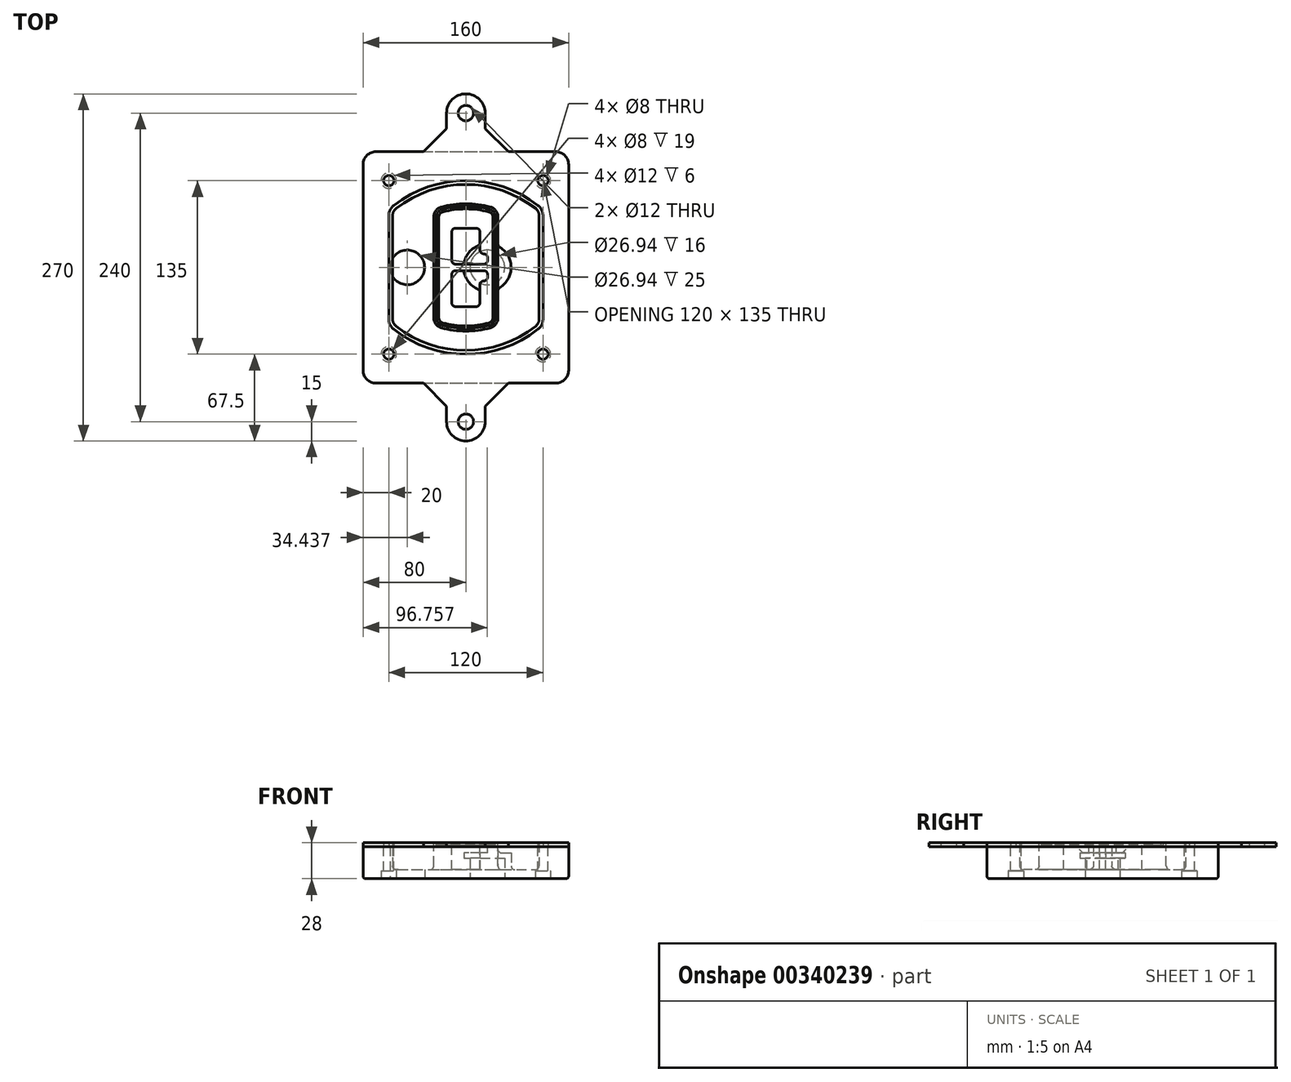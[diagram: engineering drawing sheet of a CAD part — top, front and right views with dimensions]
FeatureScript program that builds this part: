
annotation { "Feature Type Name" : "Feature", "Feature Type Description" : "" }
export const myFeature = defineFeature(function(context is Context, id is Id, definition is map)
    precondition{}
    {
        {
            var Q0;
            Q0=qCreatedBy(makeId("Top.planeOp"),FACE);
            var sketch = newSketch(context, id + "F0", { "sketchPlane" : qUnion([Q0])});
            skPoint(sketch, "E0.rect.middle", {"position": v(0, 0) * mm});
            skLineSegment(sketch, "E1.bottom", {"start": v(-70, -90) * mm, "end": v(70, -90) * mm});
            skLineSegment(sketch, "E1.top", {"start": v(-70, 90) * mm, "end": v(70, 90) * mm});
            skLineSegment(sketch, "E1.left", {"start": v(-80, -80) * mm, "end": v(-80, 80) * mm});
            skLineSegment(sketch, "E1.right", {"start": v(80, -80) * mm, "end": v(80, 80) * mm});
            skLineSegment(sketch, "E2", {"start": v(-80, 90) * mm, "end": v(80, -90) * mm, "construction": true});
            skLineSegment(sketch, "E3", {"start": v(80, 90) * mm, "end": v(-80, -90) * mm, "construction": true});
            skCircle(sketch, "E4", {"center": v(-60, 67.5) * mm, "radius": 4 * mm});
            skCircle(sketch, "E5", {"center": v(60, 67.5) * mm, "radius": 4 * mm});
            skCircle(sketch, "E6", {"center": v(60, -67.5) * mm, "radius": 4 * mm});
            skCircle(sketch, "E7", {"center": v(-60, -67.5) * mm, "radius": 4 * mm});
            skLineSegment(sketch, "E8", {"start": v(-60, 67.5) * mm, "end": v(60, 67.5) * mm, "construction": true});
            skLineSegment(sketch, "E9", {"start": v(60, 67.5) * mm, "end": v(60, -67.5) * mm, "construction": true});
            skLineSegment(sketch, "E10", {"start": v(60, -67.5) * mm, "end": v(-60, -67.5) * mm, "construction": true});
            skLineSegment(sketch, "E11", {"start": v(-60, -67.5) * mm, "end": v(-60, 67.5) * mm, "construction": true});
            skLineSegment(sketch, "E12", {"start": v(-60, 40.3) * mm, "end": v(-60, -40.3) * mm});
            skLineSegment(sketch, "E13", {"start": v(60, 40.3) * mm, "end": v(60, -40.3) * mm});
            skArc(sketch, "E14", {"start": v(56.15, 48.18) * mm, "mid": v(0, 67.5) * mm, "end": v(-56.15, 48.18) * mm});
            skArc(sketch, "E15", {"start": v(-56.15, -48.18) * mm, "mid": v(0, -67.5) * mm, "end": v(56.15, -48.18) * mm});
            skLineSegment(sketch, "E16", {"start": v(-60, 0) * mm, "end": v(60, 0) * mm, "construction": true});
            skPoint(sketch, "E17.visualSharp", {"position": v(-60, -45) * mm});
            skArc(sketch, "E17.filletArc", {"start": v(-60, -40.3) * mm, "mid": v(-58.99, -44.68) * mm, "end": v(-56.15, -48.18) * mm});
            skPoint(sketch, "E18.visualSharp", {"position": v(-60, 45) * mm});
            skArc(sketch, "E18.filletArc", {"start": v(-56.15, 48.18) * mm, "mid": v(-58.99, 44.68) * mm, "end": v(-60, 40.3) * mm});
            skPoint(sketch, "E19.visualSharp", {"position": v(60, 45) * mm});
            skArc(sketch, "E19.filletArc", {"start": v(60, 40.3) * mm, "mid": v(58.99, 44.68) * mm, "end": v(56.15, 48.18) * mm});
            skPoint(sketch, "E20.visualSharp", {"position": v(60, -45) * mm});
            skArc(sketch, "E20.filletArc", {"start": v(56.15, -48.18) * mm, "mid": v(58.99, -44.68) * mm, "end": v(60, -40.3) * mm});
            skPoint(sketch, "E21.visualSharp", {"position": v(-80, 90) * mm});
            skArc(sketch, "E21.filletArc", {"start": v(-70, 90) * mm, "mid": v(-77.07, 87.07) * mm, "end": v(-80, 80) * mm});
            skPoint(sketch, "E22.visualSharp", {"position": v(80, 90) * mm});
            skArc(sketch, "E22.filletArc", {"start": v(80, 80) * mm, "mid": v(77.07, 87.07) * mm, "end": v(70, 90) * mm});
            skPoint(sketch, "E23.visualSharp", {"position": v(80, -90) * mm});
            skArc(sketch, "E23.filletArc", {"start": v(70, -90) * mm, "mid": v(77.07, -87.07) * mm, "end": v(80, -80) * mm});
            skPoint(sketch, "E24.visualSharp", {"position": v(-80, -90) * mm});
            skArc(sketch, "E24.filletArc", {"start": v(-80, -80) * mm, "mid": v(-77.07, -87.07) * mm, "end": v(-70, -90) * mm});
            skArc(sketch, "E25.0", {"start": v(57, 40.3) * mm, "mid": v(56.3, 43.36) * mm, "end": v(54.3, 45.81) * mm});
            skLineSegment(sketch, "E25.1", {"start": v(57, 40.3) * mm, "end": v(57, -40.3) * mm});
            skArc(sketch, "E25.2", {"start": v(54.3, -45.81) * mm, "mid": v(56.3, -43.36) * mm, "end": v(57, -40.3) * mm});
            skArc(sketch, "E25.3", {"start": v(-54.3, -45.81) * mm, "mid": v(0, -64.5) * mm, "end": v(54.3, -45.81) * mm});
            skArc(sketch, "E25.4", {"start": v(-57, -40.3) * mm, "mid": v(-56.3, -43.36) * mm, "end": v(-54.3, -45.81) * mm});
            skArc(sketch, "E25.5", {"start": v(54.3, 45.81) * mm, "mid": v(0, 64.5) * mm, "end": v(-54.3, 45.81) * mm});
            skLineSegment(sketch, "E25.6", {"start": v(-57, 40.3) * mm, "end": v(-57, -40.3) * mm});
            skArc(sketch, "E25.7", {"start": v(-54.3, 45.81) * mm, "mid": v(-56.3, 43.36) * mm, "end": v(-57, 40.3) * mm});
            skArc(sketch, "E26.0", {"start": v(-58.62, 51.33) * mm, "mid": v(-62.58, 46.43) * mm, "end": v(-64, 40.3) * mm});
            skArc(sketch, "E26.1", {"start": v(58.62, 51.33) * mm, "mid": v(0, 71.5) * mm, "end": v(-58.62, 51.33) * mm});
            skArc(sketch, "E26.2", {"start": v(64, 40.3) * mm, "mid": v(62.58, 46.43) * mm, "end": v(58.62, 51.33) * mm});
            skLineSegment(sketch, "E26.3", {"start": v(64, 40.3) * mm, "end": v(64, -40.3) * mm});
            skArc(sketch, "E26.4", {"start": v(58.62, -51.33) * mm, "mid": v(62.58, -46.43) * mm, "end": v(64, -40.3) * mm});
            skLineSegment(sketch, "E26.5", {"start": v(-64, 40.3) * mm, "end": v(-64, -40.3) * mm});
            skArc(sketch, "E26.6", {"start": v(-58.62, -51.33) * mm, "mid": v(0, -71.5) * mm, "end": v(58.62, -51.33) * mm});
            skArc(sketch, "E26.7", {"start": v(-64, -40.3) * mm, "mid": v(-62.58, -46.43) * mm, "end": v(-58.62, -51.33) * mm});
            skSolve(sketch);
        }
        {
            var Q0;
            Q0=makeQuery(id+"F0.imprint","IMPRINT",FACE,{"disambiguationData":[TD([[makeQuery(id+"F0.imprint","IMPRINT",EDGE,{"derivedFrom":sQuery(id+"F0.wireOp",EDGE,"E1.bottom")}),1.0]])]});
            var Q1;
            Q1=makeQuery(id+"F0.imprint","IMPRINT",FACE,{"disambiguationData":[TD([[makeQuery(id+"F0.imprint","IMPRINT",EDGE,{"derivedFrom":sQuery(id+"F0.wireOp",EDGE,"E12")}),1.0]])]});
            var Q2;
            Q2=makeQuery(id+"F0.imprint","IMPRINT",FACE,{"disambiguationData":[TD([[makeQuery(id+"F0.imprint","IMPRINT",EDGE,{"derivedFrom":sQuery(id+"F0.wireOp",EDGE,"E25.0")}),1.0]])]});
            var Q3;
            Q3=makeQuery(id+"F0.imprint","IMPRINT",FACE,{"disambiguationData":[TD([[makeQuery(id+"F0.imprint","IMPRINT",EDGE,{"derivedFrom":sQuery(id+"F0.wireOp",EDGE,"E12")}),-1.0]])]});
            extrude(context, id + "F1", {"entities" : qUnion([Q0, Q1, Q2, Q3]), "oppositeDirection" : true, "depth" : 25 * mm});
        }
        {
            var Q0;
            Q0=makeQuery(id+"F0.imprint","IMPRINT",FACE,{"disambiguationData":[TD([[makeQuery(id+"F0.imprint","IMPRINT",EDGE,{"derivedFrom":sQuery(id+"F0.wireOp",EDGE,"E12")}),1.0]])]});
            extrude(context, id + "F2", {"entities" : qUnion([Q0]), "operationType" : NewBodyOperationType.ADD, "depth" : 3 * mm});
        }
        {
            var Q0;
            Q0=makeQuery(id+"F0.imprint","IMPRINT",FACE,{"disambiguationData":[TD([[makeQuery(id+"F0.imprint","IMPRINT",EDGE,{"derivedFrom":sQuery(id+"F0.wireOp",EDGE,"E25.0")}),1.0]])]});
            extrude(context, id + "F3", {"entities" : qUnion([Q0]), "operationType" : NewBodyOperationType.REMOVE, "oppositeDirection" : true, "depth" : 18 * mm});
        }
        {
            var Q0;
            Q0=makeQuery(id+"F2.opExtrude","CAP_FACE",FACE,{"disambiguationData":[OSD([sQuery(id+"F0.wireOp",EDGE,"E12"),sQuery(id+"F0.wireOp",EDGE,"E13"),sQuery(id+"F0.wireOp",EDGE,"E14"),sQuery(id+"F0.wireOp",EDGE,"E15"),sQuery(id+"F0.wireOp",EDGE,"E17.filletArc"),sQuery(id+"F0.wireOp",EDGE,"E18.filletArc"),sQuery(id+"F0.wireOp",EDGE,"E19.filletArc"),sQuery(id+"F0.wireOp",EDGE,"E20.filletArc"),sQuery(id+"F0.wireOp",EDGE,"E25.0"),sQuery(id+"F0.wireOp",EDGE,"E25.1"),sQuery(id+"F0.wireOp",EDGE,"E25.2"),sQuery(id+"F0.wireOp",EDGE,"E25.3"),sQuery(id+"F0.wireOp",EDGE,"E25.4"),sQuery(id+"F0.wireOp",EDGE,"E25.5"),sQuery(id+"F0.wireOp",EDGE,"E25.6"),sQuery(id+"F0.wireOp",EDGE,"E25.7")])],"isStart":false});
            var sketch = newSketch(context, id + "F4", { "sketchPlane" : qUnion([Q0])});
            skArc(sketch, "E27.0", {"start": v(-19.08, -46.97) * mm, "mid": v(0, -49.5) * mm, "end": v(19.08, -46.97) * mm});
            skArc(sketch, "E28.0", {"start": v(19.08, 46.97) * mm, "mid": v(0, 49.5) * mm, "end": v(-19.08, 46.97) * mm});
            skLineSegment(sketch, "E29", {"start": v(-25, 39.25) * mm, "end": v(-25, -39.25) * mm});
            skLineSegment(sketch, "E30", {"start": v(25, 39.25) * mm, "end": v(25, -39.25) * mm});
            skLineSegment(sketch, "E31", {"start": v(-25, 45.1) * mm, "end": v(25, 45.1) * mm, "construction": true});
            skLineSegment(sketch, "E32", {"start": v(-25, -45.1) * mm, "end": v(25, -45.1) * mm, "construction": true});
            skPoint(sketch, "E33.visualSharp", {"position": v(-25, 45.1) * mm});
            skArc(sketch, "E33.filletArc", {"start": v(-19.08, 46.97) * mm, "mid": v(-23.35, 44.11) * mm, "end": v(-25, 39.25) * mm});
            skPoint(sketch, "E34.visualSharp", {"position": v(25, 45.1) * mm});
            skArc(sketch, "E34.filletArc", {"start": v(25, 39.25) * mm, "mid": v(23.35, 44.11) * mm, "end": v(19.08, 46.97) * mm});
            skPoint(sketch, "E35.visualSharp", {"position": v(25, -45.1) * mm});
            skArc(sketch, "E35.filletArc", {"start": v(19.08, -46.97) * mm, "mid": v(23.35, -44.11) * mm, "end": v(25, -39.25) * mm});
            skPoint(sketch, "E36.visualSharp", {"position": v(-25, -45.1) * mm});
            skArc(sketch, "E36.filletArc", {"start": v(-25, -39.25) * mm, "mid": v(-23.35, -44.11) * mm, "end": v(-19.08, -46.97) * mm});
            skArc(sketch, "E37.0", {"start": v(54.3, 45.81) * mm, "mid": v(0, 64.5) * mm, "end": v(-54.3, 45.81) * mm});
            skArc(sketch, "E37.1", {"start": v(-54.3, 45.81) * mm, "mid": v(-56.3, 43.36) * mm, "end": v(-57, 40.3) * mm});
            skLineSegment(sketch, "E37.2", {"start": v(-57, 40.3) * mm, "end": v(-57, -40.3) * mm});
            skArc(sketch, "E37.3", {"start": v(-57, -40.3) * mm, "mid": v(-56.3, -43.36) * mm, "end": v(-54.3, -45.81) * mm});
            skArc(sketch, "E37.4", {"start": v(-54.3, -45.81) * mm, "mid": v(0, -64.5) * mm, "end": v(54.3, -45.81) * mm});
            skArc(sketch, "E37.5", {"start": v(54.3, -45.81) * mm, "mid": v(56.3, -43.36) * mm, "end": v(57, -40.3) * mm});
            skLineSegment(sketch, "E37.6", {"start": v(57, 40.3) * mm, "end": v(57, -40.3) * mm});
            skArc(sketch, "E37.7", {"start": v(57, 40.3) * mm, "mid": v(56.3, 43.36) * mm, "end": v(54.3, 45.81) * mm});
            skLineSegment(sketch, "E38.0", {"start": v(23, 39.25) * mm, "end": v(23, -39.25) * mm});
            skArc(sketch, "E38.1", {"start": v(18.56, -45.04) * mm, "mid": v(21.76, -42.9) * mm, "end": v(23, -39.25) * mm});
            skArc(sketch, "E38.2", {"start": v(-18.56, -45.04) * mm, "mid": v(0, -47.5) * mm, "end": v(18.56, -45.04) * mm});
            skArc(sketch, "E38.3", {"start": v(-23, -39.25) * mm, "mid": v(-21.76, -42.9) * mm, "end": v(-18.56, -45.04) * mm});
            skLineSegment(sketch, "E38.4", {"start": v(-23, 39.25) * mm, "end": v(-23, -39.25) * mm});
            skArc(sketch, "E38.5", {"start": v(23, 39.25) * mm, "mid": v(21.76, 42.9) * mm, "end": v(18.56, 45.04) * mm});
            skArc(sketch, "E38.6", {"start": v(-18.56, 45.04) * mm, "mid": v(-21.76, 42.9) * mm, "end": v(-23, 39.25) * mm});
            skArc(sketch, "E38.7", {"start": v(18.56, 45.04) * mm, "mid": v(0, 47.5) * mm, "end": v(-18.56, 45.04) * mm});
            skArc(sketch, "E39.0", {"start": v(21, 39.25) * mm, "mid": v(20.18, 41.68) * mm, "end": v(18.04, 43.1) * mm});
            skLineSegment(sketch, "E39.1", {"start": v(21, 39.25) * mm, "end": v(21, -39.25) * mm});
            skArc(sketch, "E39.2", {"start": v(18.04, -43.1) * mm, "mid": v(20.18, -41.68) * mm, "end": v(21, -39.25) * mm});
            skArc(sketch, "E39.3", {"start": v(-18.04, -43.1) * mm, "mid": v(0, -45.5) * mm, "end": v(18.04, -43.1) * mm});
            skArc(sketch, "E39.4", {"start": v(-21, -39.25) * mm, "mid": v(-20.18, -41.68) * mm, "end": v(-18.04, -43.1) * mm});
            skArc(sketch, "E39.5", {"start": v(18.04, 43.1) * mm, "mid": v(0, 45.5) * mm, "end": v(-18.04, 43.1) * mm});
            skLineSegment(sketch, "E39.6", {"start": v(-21, 39.25) * mm, "end": v(-21, -39.25) * mm});
            skArc(sketch, "E39.7", {"start": v(-18.04, 43.1) * mm, "mid": v(-20.18, 41.68) * mm, "end": v(-21, 39.25) * mm});
            skLineSegment(sketch, "E40", {"start": v(-25, 0) * mm, "end": v(25, 0) * mm, "construction": true});
            skLineSegment(sketch, "E41", {"start": v(-11, 5.5) * mm, "end": v(-11, 27.5) * mm});
            skLineSegment(sketch, "E42", {"start": v(-8, 30.5) * mm, "end": v(8, 30.5) * mm});
            skLineSegment(sketch, "E43", {"start": v(11, 27.5) * mm, "end": v(11, 13.5) * mm});
            skLineSegment(sketch, "E44", {"start": v(14, 10.5) * mm, "end": v(14, 10.5) * mm});
            skLineSegment(sketch, "E45", {"start": v(17, 7.5) * mm, "end": v(17, 5.5) * mm});
            skLineSegment(sketch, "E46", {"start": v(14, 2.5) * mm, "end": v(-8, 2.5) * mm});
            skPoint(sketch, "E47.visualSharp", {"position": v(-11, 30.5) * mm});
            skArc(sketch, "E47.filletArc", {"start": v(-8, 30.5) * mm, "mid": v(-10.12, 29.62) * mm, "end": v(-11, 27.5) * mm});
            skPoint(sketch, "E48.visualSharp", {"position": v(11, 30.5) * mm});
            skArc(sketch, "E48.filletArc", {"start": v(11, 27.5) * mm, "mid": v(10.12, 29.62) * mm, "end": v(8, 30.5) * mm});
            skPoint(sketch, "E49.visualSharp", {"position": v(11, 10.5) * mm});
            skArc(sketch, "E49.filletArc", {"start": v(11, 13.5) * mm, "mid": v(11.88, 11.38) * mm, "end": v(14, 10.5) * mm});
            skPoint(sketch, "E50.visualSharp", {"position": v(17, 10.5) * mm});
            skArc(sketch, "E50.filletArc", {"start": v(17, 7.5) * mm, "mid": v(16.12, 9.62) * mm, "end": v(14, 10.5) * mm});
            skPoint(sketch, "E51.visualSharp", {"position": v(17, 2.5) * mm});
            skArc(sketch, "E51.filletArc", {"start": v(14, 2.5) * mm, "mid": v(16.12, 3.38) * mm, "end": v(17, 5.5) * mm});
            skPoint(sketch, "E52.visualSharp", {"position": v(-11, 2.5) * mm});
            skArc(sketch, "E52.filletArc", {"start": v(-11, 5.5) * mm, "mid": v(-10.12, 3.38) * mm, "end": v(-8, 2.5) * mm});
            skLineSegment(sketch, "E53.0.MirrorCS", {"start": v(14, -2.5) * mm, "end": v(-8, -2.5) * mm});
            skArc(sketch, "E54.0.MirrorCS", {"start": v(-11, -5.5) * mm, "mid": v(-10.12, -3.38) * mm, "end": v(-8, -2.5) * mm});
            skLineSegment(sketch, "E55.0.MirrorCS", {"start": v(-11, -5.5) * mm, "end": v(-11, -27.5) * mm});
            skArc(sketch, "E56.0.MirrorCS", {"start": v(-8, -30.5) * mm, "mid": v(-10.12, -29.62) * mm, "end": v(-11, -27.5) * mm});
            skLineSegment(sketch, "E57.0.MirrorCS", {"start": v(-8, -30.5) * mm, "end": v(8, -30.5) * mm});
            skArc(sketch, "E58.0.MirrorCS", {"start": v(11, -27.5) * mm, "mid": v(10.12, -29.62) * mm, "end": v(8, -30.5) * mm});
            skLineSegment(sketch, "E59.0.MirrorCS", {"start": v(11, -27.5) * mm, "end": v(11, -13.5) * mm});
            skArc(sketch, "E60.0.MirrorCS", {"start": v(11, -13.5) * mm, "mid": v(11.88, -11.38) * mm, "end": v(14, -10.5) * mm});
            skArc(sketch, "E61.0.MirrorCS", {"start": v(17, -7.5) * mm, "mid": v(16.12, -9.62) * mm, "end": v(14, -10.5) * mm});
            skLineSegment(sketch, "E62.0.MirrorCS", {"start": v(17, -7.5) * mm, "end": v(17, -5.5) * mm});
            skArc(sketch, "E63.0.MirrorCS", {"start": v(14, -2.5) * mm, "mid": v(16.12, -3.38) * mm, "end": v(17, -5.5) * mm});
            skSolve(sketch);
        }
        {
            var Q0;
            Q0=makeQuery(id+"F4.imprint","IMPRINT",FACE,{"disambiguationData":[TD([[makeQuery(id+"F4.imprint","IMPRINT",EDGE,{"derivedFrom":sQuery(id+"F4.wireOp",EDGE,"E27.0")}),1.0]])]});
            var Q1;
            Q1=makeQuery(id+"F4.imprint","IMPRINT",FACE,{"disambiguationData":[TD([[makeQuery(id+"F4.imprint","IMPRINT",EDGE,{"derivedFrom":sQuery(id+"F4.wireOp",EDGE,"E38.0")}),-1.0]])]});
            var Q2;
            Q2=makeQuery(id+"F4.imprint","IMPRINT",FACE,{"disambiguationData":[TD([[makeQuery(id+"F4.imprint","IMPRINT",EDGE,{"derivedFrom":sQuery(id+"F4.wireOp",EDGE,"E39.0")}),1.0]])]});
            extrude(context, id + "F5", {"entities" : qUnion([Q0, Q1, Q2]), "operationType" : NewBodyOperationType.ADD, "endBound" : BoundingType.UP_TO_NEXT, "oppositeDirection" : true, "depth" : 25 * mm});
        }
        {
            var Q0;
            Q0=makeQuery(id+"F4.imprint","IMPRINT",FACE,{"disambiguationData":[TD([[makeQuery(id+"F4.imprint","IMPRINT",EDGE,{"derivedFrom":sQuery(id+"F4.wireOp",EDGE,"E38.0")}),-1.0]])]});
            extrude(context, id + "F6", {"entities" : qUnion([Q0]), "operationType" : NewBodyOperationType.REMOVE, "oppositeDirection" : true, "depth" : 2 * mm});
        }
        {
            var Q0;
            Q0=makeQuery(id+"F1.opExtrude","CAP_FACE",FACE,{"disambiguationData":[OSD([sQuery(id+"F0.wireOp",EDGE,"E1.bottom"),sQuery(id+"F0.wireOp",EDGE,"E1.top"),sQuery(id+"F0.wireOp",EDGE,"E1.left"),sQuery(id+"F0.wireOp",EDGE,"E1.right"),sQuery(id+"F0.wireOp",EDGE,"E4"),sQuery(id+"F0.wireOp",EDGE,"E5"),sQuery(id+"F0.wireOp",EDGE,"E6"),sQuery(id+"F0.wireOp",EDGE,"E7"),sQuery(id+"F0.wireOp",EDGE,"E21.filletArc"),sQuery(id+"F0.wireOp",EDGE,"E22.filletArc"),sQuery(id+"F0.wireOp",EDGE,"E23.filletArc"),sQuery(id+"F0.wireOp",EDGE,"E24.filletArc")])],"isStart":false});
            var sketch = newSketch(context, id + "F7", { "sketchPlane" : qUnion([Q0])});
            skCircle(sketch, "E64", {"center": v(16.76, 0) * mm, "radius": 13.47 * mm});
            skCircle(sketch, "E65", {"center": v(-45.56, 0) * mm, "radius": 13.47 * mm});
            skLineSegment(sketch, "E66", {"start": v(80, 0) * mm, "end": v(-80, 0) * mm});
            skCircle(sketch, "E67", {"center": v(16.76, 0) * mm, "radius": 18.47 * mm});
            skCircle(sketch, "E68", {"center": v(60, -67.5) * mm, "radius": 6 * mm});
            skCircle(sketch, "E69", {"center": v(-60, -67.5) * mm, "radius": 6 * mm});
            skCircle(sketch, "E70", {"center": v(-60, 67.5) * mm, "radius": 6 * mm});
            skCircle(sketch, "E71", {"center": v(60, 67.5) * mm, "radius": 6 * mm});
            skSolve(sketch);
        }
        {
            var Q0;
            {var subQ1=sQuery(id+"F7.wireOp",EDGE,"E66");var subQ4=sQuery(id+"F7.wireOp",EDGE,"E64");var subQ6=makeQuery(id+"F7.imprint","INTERSECT",VERTEX,{"disambiguationData":[OD(0.0)],"derivedFrom":[subQ4,subQ1]});Q0=makeQuery(id+"F7.imprint","IMPRINT",FACE,{"disambiguationData":[TD([[makeQuery(id+"F7.imprint","IMPRINT",EDGE,{"disambiguationData":[TD([[subQ6,-1.0]])],"derivedFrom":subQ4}),-1.0]])]});}
            var Q1;
            {var subQ0=sQuery(id+"F7.wireOp",EDGE,"E66");var subQ1=sQuery(id+"F7.wireOp",EDGE,"E64");var subQ3=makeQuery(id+"F7.imprint","INTERSECT",VERTEX,{"disambiguationData":[OD(0.0)],"derivedFrom":[subQ1,subQ0]});Q1=makeQuery(id+"F7.imprint","IMPRINT",FACE,{"disambiguationData":[TD([[makeQuery(id+"F7.imprint","IMPRINT",EDGE,{"disambiguationData":[TD([[subQ3,-1.0]])],"derivedFrom":subQ1}),1.0]])]});}
            var Q2;
            {var subQ0=sQuery(id+"F7.wireOp",EDGE,"E66");var subQ1=sQuery(id+"F7.wireOp",EDGE,"E64");var subQ3=makeQuery(id+"F7.imprint","INTERSECT",VERTEX,{"disambiguationData":[OD(0.0)],"derivedFrom":[subQ1,subQ0]});Q2=makeQuery(id+"F7.imprint","IMPRINT",FACE,{"disambiguationData":[TD([[makeQuery(id+"F7.imprint","IMPRINT",EDGE,{"disambiguationData":[TD([[subQ3,1.0]])],"derivedFrom":subQ1}),1.0]])]});}
            var Q3;
            {var subQ1=sQuery(id+"F7.wireOp",EDGE,"E66");var subQ4=sQuery(id+"F7.wireOp",EDGE,"E64");var subQ6=makeQuery(id+"F7.imprint","INTERSECT",VERTEX,{"disambiguationData":[OD(0.0)],"derivedFrom":[subQ4,subQ1]});Q3=makeQuery(id+"F7.imprint","IMPRINT",FACE,{"disambiguationData":[TD([[makeQuery(id+"F7.imprint","IMPRINT",EDGE,{"disambiguationData":[TD([[subQ6,1.0]])],"derivedFrom":subQ4}),-1.0]])]});}
            extrude(context, id + "F8", {"entities" : qUnion([Q0, Q1, Q2, Q3]), "operationType" : NewBodyOperationType.ADD, "oppositeDirection" : true, "depth" : 20 * mm});
        }
        {
            var Q0;
            {var subQ0=sQuery(id+"F7.wireOp",EDGE,"E66");var subQ1=sQuery(id+"F7.wireOp",EDGE,"E64");var subQ3=makeQuery(id+"F7.imprint","INTERSECT",VERTEX,{"disambiguationData":[OD(0.0)],"derivedFrom":[subQ1,subQ0]});Q0=makeQuery(id+"F7.imprint","IMPRINT",FACE,{"disambiguationData":[TD([[makeQuery(id+"F7.imprint","IMPRINT",EDGE,{"disambiguationData":[TD([[subQ3,-1.0]])],"derivedFrom":subQ1}),1.0]])]});}
            var Q1;
            {var subQ0=sQuery(id+"F7.wireOp",EDGE,"E66");var subQ1=sQuery(id+"F7.wireOp",EDGE,"E64");var subQ3=makeQuery(id+"F7.imprint","INTERSECT",VERTEX,{"disambiguationData":[OD(0.0)],"derivedFrom":[subQ1,subQ0]});Q1=makeQuery(id+"F7.imprint","IMPRINT",FACE,{"disambiguationData":[TD([[makeQuery(id+"F7.imprint","IMPRINT",EDGE,{"disambiguationData":[TD([[subQ3,1.0]])],"derivedFrom":subQ1}),1.0]])]});}
            extrude(context, id + "F9", {"entities" : qUnion([Q0, Q1]), "operationType" : NewBodyOperationType.REMOVE, "oppositeDirection" : true, "depth" : 16 * mm});
        }
        {
            var Q0;
            {var subQ0=sQuery(id+"F7.wireOp",EDGE,"E66");var subQ1=sQuery(id+"F7.wireOp",EDGE,"E65");var subQ3=makeQuery(id+"F7.imprint","INTERSECT",VERTEX,{"disambiguationData":[OD(0.0)],"derivedFrom":[subQ1,subQ0]});Q0=makeQuery(id+"F7.imprint","IMPRINT",FACE,{"disambiguationData":[TD([[makeQuery(id+"F7.imprint","IMPRINT",EDGE,{"disambiguationData":[TD([[subQ3,-1.0]])],"derivedFrom":subQ1}),1.0]])]});}
            var Q1;
            {var subQ0=sQuery(id+"F7.wireOp",EDGE,"E66");var subQ1=sQuery(id+"F7.wireOp",EDGE,"E65");var subQ3=makeQuery(id+"F7.imprint","INTERSECT",VERTEX,{"disambiguationData":[OD(0.0)],"derivedFrom":[subQ1,subQ0]});Q1=makeQuery(id+"F7.imprint","IMPRINT",FACE,{"disambiguationData":[TD([[makeQuery(id+"F7.imprint","IMPRINT",EDGE,{"disambiguationData":[TD([[subQ3,1.0]])],"derivedFrom":subQ1}),1.0]])]});}
            extrude(context, id + "F10", {"entities" : qUnion([Q0, Q1]), "operationType" : NewBodyOperationType.REMOVE, "oppositeDirection" : true, "depth" : 25 * mm});
        }
        {
            var Q0;
            Q0=makeQuery(id+"F7.imprint","IMPRINT",FACE,{"disambiguationData":[TD([[makeQuery(id+"F7.imprint","IMPRINT",EDGE,{"derivedFrom":sQuery(id+"F7.wireOp",EDGE,"E68")}),1.0]])]});
            var Q1;
            Q1=makeQuery(id+"F7.imprint","IMPRINT",FACE,{"disambiguationData":[TD([[makeQuery(id+"F7.imprint","IMPRINT",EDGE,{"derivedFrom":makeQuery(id+"F1.opExtrude","CAP_EDGE",EDGE,{"disambiguationData":[OSD([sQuery(id+"F0.wireOp",EDGE,"E5")])],"isStart":false})}),-1.0]])]});
            var Q2;
            Q2=makeQuery(id+"F7.imprint","IMPRINT",FACE,{"disambiguationData":[TD([[makeQuery(id+"F7.imprint","IMPRINT",EDGE,{"derivedFrom":sQuery(id+"F7.wireOp",EDGE,"E69")}),1.0]])]});
            var Q3;
            Q3=makeQuery(id+"F7.imprint","IMPRINT",FACE,{"disambiguationData":[TD([[makeQuery(id+"F7.imprint","IMPRINT",EDGE,{"derivedFrom":makeQuery(id+"F1.opExtrude","CAP_EDGE",EDGE,{"disambiguationData":[OSD([sQuery(id+"F0.wireOp",EDGE,"E4")])],"isStart":false})}),-1.0]])]});
            var Q4;
            Q4=makeQuery(id+"F7.imprint","IMPRINT",FACE,{"disambiguationData":[TD([[makeQuery(id+"F7.imprint","IMPRINT",EDGE,{"derivedFrom":sQuery(id+"F7.wireOp",EDGE,"E70")}),1.0]])]});
            var Q5;
            Q5=makeQuery(id+"F7.imprint","IMPRINT",FACE,{"disambiguationData":[TD([[makeQuery(id+"F7.imprint","IMPRINT",EDGE,{"derivedFrom":makeQuery(id+"F1.opExtrude","CAP_EDGE",EDGE,{"disambiguationData":[OSD([sQuery(id+"F0.wireOp",EDGE,"E7")])],"isStart":false})}),-1.0]])]});
            var Q6;
            Q6=makeQuery(id+"F7.imprint","IMPRINT",FACE,{"disambiguationData":[TD([[makeQuery(id+"F7.imprint","IMPRINT",EDGE,{"derivedFrom":sQuery(id+"F7.wireOp",EDGE,"E71")}),1.0]])]});
            var Q7;
            Q7=makeQuery(id+"F7.imprint","IMPRINT",FACE,{"disambiguationData":[TD([[makeQuery(id+"F7.imprint","IMPRINT",EDGE,{"derivedFrom":makeQuery(id+"F1.opExtrude","CAP_EDGE",EDGE,{"disambiguationData":[OSD([sQuery(id+"F0.wireOp",EDGE,"E6")])],"isStart":false})}),-1.0]])]});
            extrude(context, id + "F11", {"entities" : qUnion([Q0, Q1, Q2, Q3, Q4, Q5, Q6, Q7]), "operationType" : NewBodyOperationType.REMOVE, "oppositeDirection" : true, "depth" : 6 * mm});
        }
        {
            var Q0;
            Q0=makeQuery(id+"F9.boolean.opBoolean","COPY",FACE,{"derivedFrom":makeQuery(id+"F9.opExtrude","CAP_FACE",FACE,{"disambiguationData":[OSD([sQuery(id+"F7.wireOp",EDGE,"E64")])],"isStart":false})});
            var sketch = newSketch(context, id + "F12", { "sketchPlane" : qUnion([Q0])});
            skArc(sketch, "E72.0", {"start": v(11, 17.55) * mm, "mid": v(2.57, 11.82) * mm, "end": v(-1.54, 2.5) * mm});
            skArc(sketch, "E72.1", {"start": v(-1.54, -2.5) * mm, "mid": v(2.57, -11.82) * mm, "end": v(11, -17.55) * mm});
            skLineSegment(sketch, "E73", {"start": v(-1.54, -2.5) * mm, "end": v(14, -2.5) * mm});
            skLineSegment(sketch, "E74.0", {"start": v(14, 2.5) * mm, "end": v(-1.54, 2.5) * mm});
            skArc(sketch, "E74.1", {"start": v(14, 2.5) * mm, "mid": v(16.12, 3.38) * mm, "end": v(17, 5.5) * mm});
            skLineSegment(sketch, "E74.2", {"start": v(17, 7.5) * mm, "end": v(17, 5.5) * mm});
            skArc(sketch, "E74.3", {"start": v(17, 7.5) * mm, "mid": v(16.12, 9.62) * mm, "end": v(14, 10.5) * mm});
            skArc(sketch, "E74.4", {"start": v(11, 13.5) * mm, "mid": v(11.88, 11.38) * mm, "end": v(14, 10.5) * mm});
            skLineSegment(sketch, "E74.5", {"start": v(11, 17.55) * mm, "end": v(11, 13.5) * mm});
            skLineSegment(sketch, "E74.7", {"start": v(14, -2.5) * mm, "end": v(-1.54, -2.5) * mm});
            skArc(sketch, "E74.8", {"start": v(14, -2.5) * mm, "mid": v(16.12, -3.38) * mm, "end": v(17, -5.5) * mm});
            skLineSegment(sketch, "E74.9", {"start": v(17, -7.5) * mm, "end": v(17, -5.5) * mm});
            skArc(sketch, "E74.10", {"start": v(17, -7.5) * mm, "mid": v(16.12, -9.62) * mm, "end": v(14, -10.5) * mm});
            skArc(sketch, "E74.11", {"start": v(11, -13.5) * mm, "mid": v(11.88, -11.38) * mm, "end": v(14, -10.5) * mm});
            skLineSegment(sketch, "E74.12", {"start": v(11, -17.55) * mm, "end": v(11, -13.5) * mm});
            skPoint(sketch, "E75.orphan", {"position": v(11, -27.5) * mm});
            skPoint(sketch, "E76.orphan", {"position": v(-8, -2.5) * mm});
            skPoint(sketch, "E77.orphan", {"position": v(-8, 2.5) * mm});
            skPoint(sketch, "E78.orphan", {"position": v(11, 27.5) * mm});
            skSolve(sketch);
        }
        {
            var Q0;
            {var subQ7=sQuery(id+"F12.wireOp",EDGE,"E72.0");var subQ14=sQuery(id+"F12.wireOp",EDGE,"E72.1");var subQ16=sQuery(id+"F12.wireOp",EDGE,"E74.1");var subQ18=sQuery(id+"F12.wireOp",EDGE,"E74.8");Q0=qUnion([makeQuery(id+"F12.imprint","IMPRINT",FACE,{"disambiguationData":[TD([[makeQuery(id+"F12.imprint","IMPRINT",EDGE,{"derivedFrom":subQ7}),1.0]])]}),makeQuery(id+"F12.imprint","IMPRINT",FACE,{"disambiguationData":[TD([[makeQuery(id+"F12.imprint","IMPRINT",EDGE,{"derivedFrom":subQ14}),1.0]])]}),makeQuery(id+"F12.imprint","IMPRINT",FACE,{"disambiguationData":[TD([[makeQuery(id+"F12.imprint","IMPRINT",EDGE,{"derivedFrom":subQ16}),1.0]])]}),makeQuery(id+"F12.imprint","IMPRINT",FACE,{"disambiguationData":[TD([[makeQuery(id+"F12.imprint","IMPRINT",EDGE,{"derivedFrom":subQ18}),-1.0]])]})]);}
            var Q1;
            Q1=makeQuery(id+"F5.boolean.opBoolean","SPLIT",FACE,{"disambiguationData":[TD([makeQuery(id+"F5.opExtrude","SWEPT_FACE",FACE,{"disambiguationData":[OSD([sQuery(id+"F4.wireOp",EDGE,"E41")])]})])],"derivedFrom":makeQuery(id+"F3.boolean.opBoolean","COPY",FACE,{"derivedFrom":makeQuery(id+"F3.opExtrude","CAP_FACE",FACE,{"disambiguationData":[OSD([sQuery(id+"F0.wireOp",EDGE,"E25.0"),sQuery(id+"F0.wireOp",EDGE,"E25.1"),sQuery(id+"F0.wireOp",EDGE,"E25.2"),sQuery(id+"F0.wireOp",EDGE,"E25.3"),sQuery(id+"F0.wireOp",EDGE,"E25.4"),sQuery(id+"F0.wireOp",EDGE,"E25.5"),sQuery(id+"F0.wireOp",EDGE,"E25.6"),sQuery(id+"F0.wireOp",EDGE,"E25.7")])],"isStart":false})})});
            extrude(context, id + "F13", {"entities" : qUnion([Q0]), "operationType" : NewBodyOperationType.REMOVE, "endBound" : BoundingType.UP_TO_SURFACE, "endBoundEntityFace" : qUnion([Q1]), "depth" : 25 * mm});
        }
        {
            var Q0;
            Q0=makeQuery(id+"F3.boolean.opBoolean","COPY",EDGE,{"derivedFrom":makeQuery(id+"F3.opExtrude","CAP_EDGE",EDGE,{"disambiguationData":[OSD([sQuery(id+"F0.wireOp",EDGE,"E25.6")])],"isStart":false})});
            var Q1;
            Q1=makeQuery(id+"F8.boolean.opBoolean","INTERSECT",EDGE,{"derivedFrom":[makeQuery(id+"F5.opExtrude","SWEPT_FACE",FACE,{"disambiguationData":[OSD([sQuery(id+"F4.wireOp",EDGE,"E30")])]}),makeQuery(id+"F8.opExtrude","CAP_FACE",FACE,{"disambiguationData":[OSD([sQuery(id+"F7.wireOp",EDGE,"E67")])],"isStart":false})]});
            var Q2;
            Q2=makeQuery(id+"F8.boolean.opBoolean","INTERSECT",EDGE,{"disambiguationData":[OD(1.0)],"derivedFrom":[makeQuery(id+"F5.opExtrude","SWEPT_FACE",FACE,{"disambiguationData":[OSD([sQuery(id+"F4.wireOp",EDGE,"E30")])]}),makeQuery(id+"F8.opExtrude","SWEPT_FACE",FACE,{"disambiguationData":[OSD([sQuery(id+"F7.wireOp",EDGE,"E67")])]})]});
            var Q3;
            {var subQ0=sQuery(id+"F4.wireOp",EDGE,"E30");Q3=makeQuery(id+"F8.boolean.opBoolean","SPLIT",EDGE,{"disambiguationData":[TD([makeQuery(id+"F5.opExtrude","SWEPT_FACE",FACE,{"disambiguationData":[OSD([sQuery(id+"F4.wireOp",EDGE,"E35.filletArc")])]})])],"derivedFrom":makeQuery(id+"F5.opExtrude","CAP_EDGE",EDGE,{"disambiguationData":[OSD([subQ0])],"isStart":false})});}
            var Q4;
            {var subQ0=sQuery(id+"F0.wireOp",EDGE,"E25.7");var subQ1=sQuery(id+"F0.wireOp",EDGE,"E25.1");var subQ2=sQuery(id+"F0.wireOp",EDGE,"E25.6");var subQ3=sQuery(id+"F0.wireOp",EDGE,"E25.5");var subQ4=sQuery(id+"F0.wireOp",EDGE,"E25.4");var subQ5=sQuery(id+"F0.wireOp",EDGE,"E25.0");var subQ6=sQuery(id+"F0.wireOp",EDGE,"E25.2");var subQ7=sQuery(id+"F0.wireOp",EDGE,"E25.3");Q4=makeQuery(id+"F8.boolean.opBoolean","INTERSECT",EDGE,{"derivedFrom":[makeQuery(id+"F5.boolean.opBoolean","SPLIT",FACE,{"disambiguationData":[TD([makeQuery(id+"F2.opExtrude","SWEPT_FACE",FACE,{"disambiguationData":[OSD([subQ5])]})])],"derivedFrom":makeQuery(id+"F3.boolean.opBoolean","COPY",FACE,{"derivedFrom":makeQuery(id+"F3.opExtrude","CAP_FACE",FACE,{"disambiguationData":[OSD([subQ5,subQ1,subQ6,subQ7,subQ4,subQ3,subQ2,subQ0])],"isStart":false})})}),makeQuery(id+"F8.opExtrude","SWEPT_FACE",FACE,{"disambiguationData":[OSD([sQuery(id+"F7.wireOp",EDGE,"E67")])]})]});}
            var Q5;
            Q5=makeQuery(id+"F8.boolean.opBoolean","INTERSECT",EDGE,{"disambiguationData":[OD(0.0)],"derivedFrom":[makeQuery(id+"F5.opExtrude","SWEPT_FACE",FACE,{"disambiguationData":[OSD([sQuery(id+"F4.wireOp",EDGE,"E30")])]}),makeQuery(id+"F8.opExtrude","SWEPT_FACE",FACE,{"disambiguationData":[OSD([sQuery(id+"F7.wireOp",EDGE,"E67")])]})]});
            fillet(context, id + "F14", {"entities" : qUnion([Q0, Q1, Q2, Q3, Q4, Q5]), "radius" : 3 * mm, "tangentPropagation" : true, "allowEdgeOverflow" : false});
        }
        {
            var Q0;
            Q0=makeQuery(id+"F1.opExtrude","CAP_EDGE",EDGE,{"disambiguationData":[OSD([sQuery(id+"F0.wireOp",EDGE,"E1.bottom")])],"isStart":false});
            fillet(context, id + "F15", {"entities" : qUnion([Q0]), "radius" : 2 * mm, "tangentPropagation" : true, "allowEdgeOverflow" : false});
        }
        {
            var Q0;
            {var subQ0=sQuery(id+"F0.wireOp",EDGE,"E21.filletArc");var subQ1=sQuery(id+"F0.wireOp",EDGE,"E7");var subQ2=sQuery(id+"F0.wireOp",EDGE,"E6");var subQ3=sQuery(id+"F0.wireOp",EDGE,"E5");var subQ4=sQuery(id+"F0.wireOp",EDGE,"E4");var subQ5=sQuery(id+"F0.wireOp",EDGE,"E22.filletArc");var subQ6=sQuery(id+"F0.wireOp",EDGE,"E1.bottom");var subQ7=sQuery(id+"F0.wireOp",EDGE,"E1.right");var subQ8=sQuery(id+"F0.wireOp",EDGE,"E1.top");var subQ9=sQuery(id+"F0.wireOp",EDGE,"E1.left");var subQ10=sQuery(id+"F0.wireOp",EDGE,"E23.filletArc");var subQ11=sQuery(id+"F0.wireOp",EDGE,"E24.filletArc");Q0=makeQuery(id+"F2.boolean.opBoolean","SPLIT",FACE,{"disambiguationData":[TD([makeQuery(id+"F1.opExtrude","SWEPT_FACE",FACE,{"disambiguationData":[OSD([subQ6])]})])],"derivedFrom":makeQuery(id+"F1.opExtrude","CAP_FACE",FACE,{"disambiguationData":[OSD([subQ6,subQ8,subQ9,subQ7,subQ4,subQ3,subQ2,subQ1,subQ0,subQ5,subQ10,subQ11])],"isStart":true})});}
            var sketch = newSketch(context, id + "F16", { "sketchPlane" : qUnion([Q0])});
            skLineSegment(sketch, "E79.0", {"start": v(-70, 90) * mm, "end": v(70, 90) * mm});
            skArc(sketch, "E79.1", {"start": v(-70, 90) * mm, "mid": v(-77.07, 87.07) * mm, "end": v(-80, 80) * mm});
            skLineSegment(sketch, "E79.2", {"start": v(-80, -80) * mm, "end": v(-80, 80) * mm});
            skArc(sketch, "E79.3", {"start": v(-80, -80) * mm, "mid": v(-77.07, -87.07) * mm, "end": v(-70, -90) * mm});
            skLineSegment(sketch, "E79.4", {"start": v(-70, -90) * mm, "end": v(70, -90) * mm});
            skArc(sketch, "E79.5", {"start": v(70, -90) * mm, "mid": v(77.07, -87.07) * mm, "end": v(80, -80) * mm});
            skLineSegment(sketch, "E79.6", {"start": v(80, -80) * mm, "end": v(80, 80) * mm});
            skArc(sketch, "E79.7", {"start": v(80, 80) * mm, "mid": v(77.07, 87.07) * mm, "end": v(70, 90) * mm});
            skCircle(sketch, "E79.8", {"center": v(60, 67.5) * mm, "radius": 4 * mm});
            skCircle(sketch, "E79.9", {"center": v(-60, 67.5) * mm, "radius": 4 * mm});
            skCircle(sketch, "E79.10", {"center": v(-60, -67.5) * mm, "radius": 4 * mm});
            skCircle(sketch, "E79.11", {"center": v(60, -67.5) * mm, "radius": 4 * mm});
            skArc(sketch, "E79.12", {"start": v(56.15, 48.18) * mm, "mid": v(0, 67.5) * mm, "end": v(-56.15, 48.18) * mm});
            skLineSegment(sketch, "E79.13", {"start": v(-60, 40.3) * mm, "end": v(-60, -40.3) * mm});
            skArc(sketch, "E79.14", {"start": v(-56.15, 48.18) * mm, "mid": v(-58.99, 44.68) * mm, "end": v(-60, 40.3) * mm});
            skArc(sketch, "E79.15", {"start": v(-60, -40.3) * mm, "mid": v(-58.99, -44.68) * mm, "end": v(-56.15, -48.18) * mm});
            skArc(sketch, "E79.16", {"start": v(-56.15, -48.18) * mm, "mid": v(0, -67.5) * mm, "end": v(56.15, -48.18) * mm});
            skArc(sketch, "E79.17", {"start": v(56.15, -48.18) * mm, "mid": v(58.99, -44.68) * mm, "end": v(60, -40.3) * mm});
            skLineSegment(sketch, "E79.18", {"start": v(60, 40.3) * mm, "end": v(60, -40.3) * mm});
            skArc(sketch, "E79.19", {"start": v(60, 40.3) * mm, "mid": v(58.99, 44.68) * mm, "end": v(56.15, 48.18) * mm});
            skLineSegment(sketch, "E80", {"start": v(0, 90) * mm, "end": v(0, 120) * mm, "construction": true});
            skLineSegment(sketch, "E81", {"start": v(-15, 108) * mm, "end": v(-15, 120) * mm});
            skLineSegment(sketch, "E82", {"start": v(15, 108) * mm, "end": v(15, 120) * mm});
            skArc(sketch, "E83", {"start": v(15, 120) * mm, "mid": v(0, 135) * mm, "end": v(-15, 120) * mm});
            skLineSegment(sketch, "E84", {"start": v(-33, 90) * mm, "end": v(-15, 108) * mm});
            skCircle(sketch, "E85", {"center": v(0, 120) * mm, "radius": 6 * mm});
            skLineSegment(sketch, "E86", {"start": v(15, 108) * mm, "end": v(33, 90) * mm});
            skLineSegment(sketch, "E87", {"start": v(-80, 0) * mm, "end": v(80, 0) * mm, "construction": true});
            skLineSegment(sketch, "E88.MirrorCS", {"start": v(-15, -108) * mm, "end": v(-15, -120) * mm});
            skLineSegment(sketch, "E89.MirrorCS", {"start": v(15, -108) * mm, "end": v(15, -120) * mm});
            skCircle(sketch, "E90.MirrorC", {"center": v(0, -120) * mm, "radius": 6 * mm});
            skArc(sketch, "E91.MirrorCS", {"start": v(15, -120) * mm, "mid": v(0, -135) * mm, "end": v(-15, -120) * mm});
            skArc(sketch, "E92.MirrorCS", {"start": v(-70, -90) * mm, "mid": v(-77.07, -87.07) * mm, "end": v(-80, -80) * mm});
            skLineSegment(sketch, "E93.MirrorCS", {"start": v(-33, -90) * mm, "end": v(-15, -108) * mm});
            skArc(sketch, "E94.MirrorCS", {"start": v(80, -80) * mm, "mid": v(77.07, -87.07) * mm, "end": v(70, -90) * mm});
            skLineSegment(sketch, "E95.MirrorCS", {"start": v(15, -108) * mm, "end": v(33, -90) * mm});
            skLineSegment(sketch, "E96.MirrorCS", {"start": v(0, -90) * mm, "end": v(0, -120) * mm, "construction": true});
            skSolve(sketch);
        }
        {
            var Q0;
            Q0 = qSketchRegion(id + "F16", true);
            var Q1;
            Q1=makeQuery(id+"F2.opExtrude","CAP_FACE",FACE,{"disambiguationData":[OSD([sQuery(id+"F0.wireOp",EDGE,"E12"),sQuery(id+"F0.wireOp",EDGE,"E13"),sQuery(id+"F0.wireOp",EDGE,"E14"),sQuery(id+"F0.wireOp",EDGE,"E15"),sQuery(id+"F0.wireOp",EDGE,"E17.filletArc"),sQuery(id+"F0.wireOp",EDGE,"E18.filletArc"),sQuery(id+"F0.wireOp",EDGE,"E19.filletArc"),sQuery(id+"F0.wireOp",EDGE,"E20.filletArc"),sQuery(id+"F0.wireOp",EDGE,"E25.0"),sQuery(id+"F0.wireOp",EDGE,"E25.1"),sQuery(id+"F0.wireOp",EDGE,"E25.2"),sQuery(id+"F0.wireOp",EDGE,"E25.3"),sQuery(id+"F0.wireOp",EDGE,"E25.4"),sQuery(id+"F0.wireOp",EDGE,"E25.5"),sQuery(id+"F0.wireOp",EDGE,"E25.6"),sQuery(id+"F0.wireOp",EDGE,"E25.7")])],"isStart":false});
            extrude(context, id + "F17", {"entities" : qUnion([Q0]), "endBound" : BoundingType.UP_TO_SURFACE, "endBoundEntityFace" : qUnion([Q1]), "depth" : 25 * mm});
        }
    });
